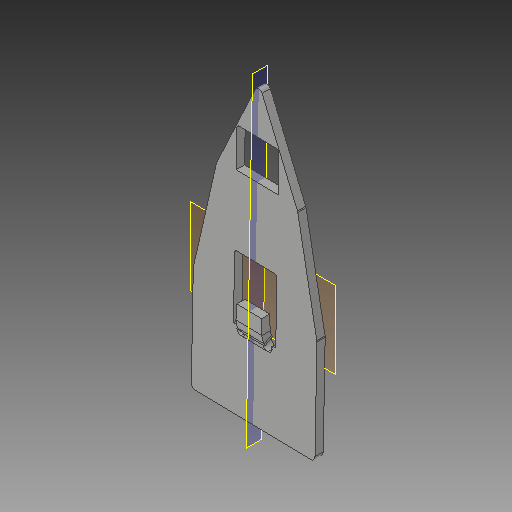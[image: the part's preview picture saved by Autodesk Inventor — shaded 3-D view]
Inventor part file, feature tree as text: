
AUTODESK INVENTOR PART (.ipt)
format: ipt  version: 2018 (Build 220112000, 112)  size: 412,160 bytes
history: native  units: mm
features: other x7, sheet_metal_op x3, sketch x3, hole x2, plane x1, fillet x1, reference x1
ambient origin geometry x8: Origin, YZ Plane, XZ Plane, XY Plane, X Axis, Y Axis, Z Axis, Center Point
bodies: Solid1 (feature_tree)
feature tree (18):
  plane  "Work Plane1"
  sheet_metal_op  "Face1"
  hole  "Hole1"  [1 undecoded]
  hole  "Hole2"  [1 undecoded]
  fillet  "Fillet1"  Radius=38.0mm
  sheet_metal_op  "Fold1"
  sheet_metal_op  "Fold2"
  other  "modtplan"
  sketch  "Sketch1"  dims[d0=8.0mm]
  other  "Plate1"
  reference  "Reference38"
  sketch  "Sketch2"  dims[d1=44.0mm d3=24.0mm d4=38.0mm d5=24.0mm d7=28.0mm d8=2.0mm]
  sketch  "Sketch3"  dims[d9=41.0mm d10=24.0mm d11=38.0mm d12=24.0mm d13=26.0mm d14=2.0mm d22=130.0mm d23=40.5mm d24=38.0mm d25=2.0mm d28=3.0mm d29=0.0mm d30=3.0mm d31=8.0mm d32=6.0mm d33=4.0mm d34=2.0mm d35=90.0deg d36=8.0mm d37=20.594885mm d38=0.0mm d39=3.0mm d40=8.0mm d41=6.0mm d42=4.0mm d43=2.0mm d44=90.0deg d45=8.0mm d46=20.594885mm d47=1.0mm d48=8.0mm d49=4.0mm d50=16.0mm d51=8.0mm d52=30.0deg d53=8.0mm d54=20.0mm d55=8.0mm d56=4.0mm d57=16.0mm d58=8.0mm d59=30.0deg d60=8.0mm]
  parser-record x1  (decoder bookkeeping rows leaked as tree rows — omitted from the tree; the rows remain in map.json)
  other  "modul top.iam"
  other  "vange top:1"
  other  "Definition1"
  other  "plade:1"
note: 2 required parameter values undecoded (feature->parameter linkage not recoverable at this tier; creation-order binding heuristic only, values carry confidence <= 0.55)
note: 1 file-system path scrubbed to <path> (originals preserved in map.json)
